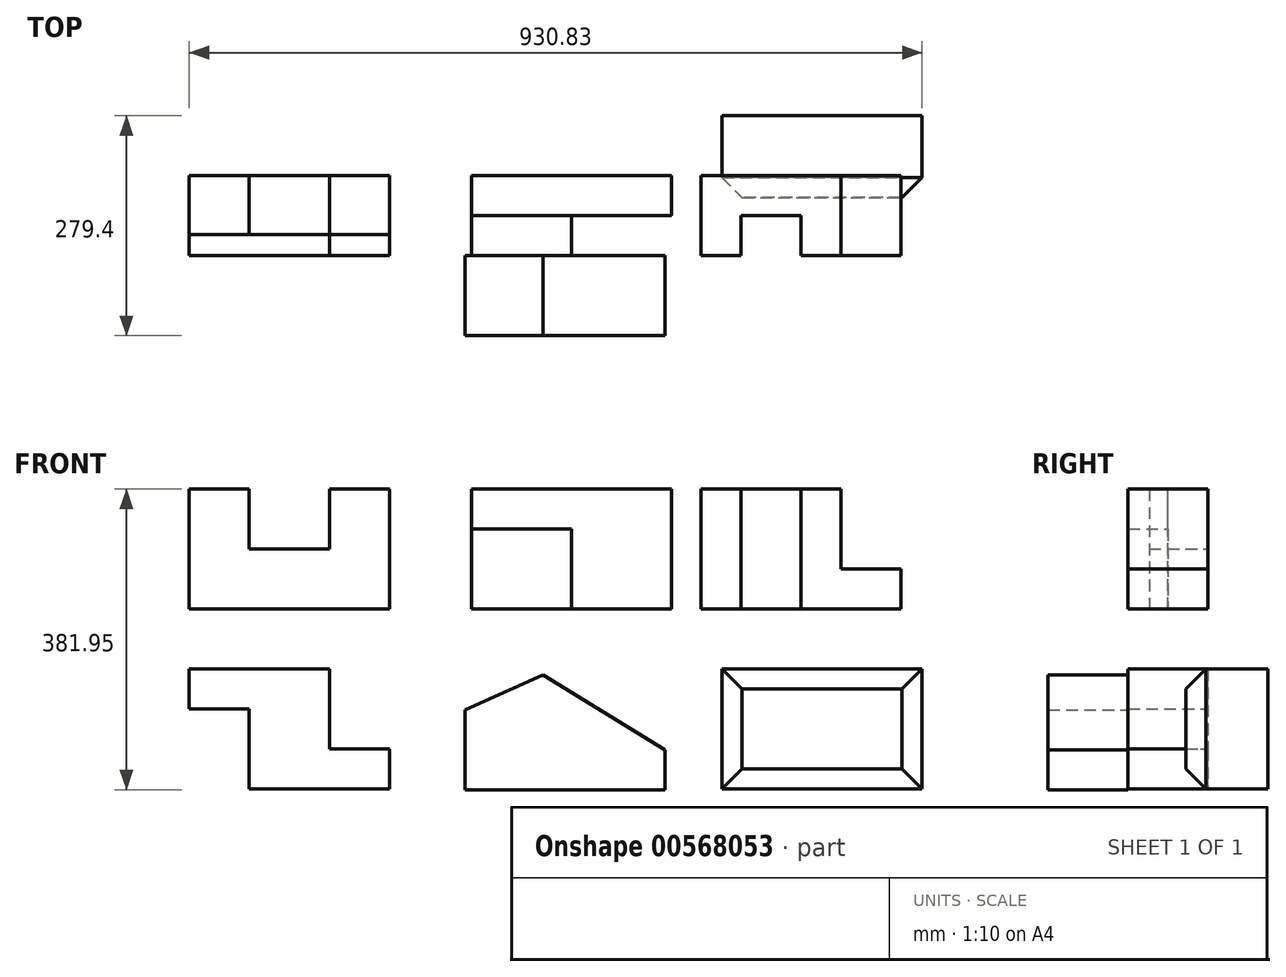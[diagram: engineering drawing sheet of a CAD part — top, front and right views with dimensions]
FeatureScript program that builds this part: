
annotation { "Feature Type Name" : "Feature", "Feature Type Description" : "" }
export const myFeature = defineFeature(function(context is Context, id is Id, definition is map)
    precondition{}
    {
        {
            var Q0;
            Q0=qCreatedBy(makeId("Front.planeOp"),FACE);
            var sketch = newSketch(context, id + "F0", { "sketchPlane" : qUnion([Q0])});
            skLineSegment(sketch, "E0", {"start": v(0, 0) * mm, "end": v(254, 0) * mm});
            skLineSegment(sketch, "E1", {"start": v(254, 0) * mm, "end": v(254, 152.4) * mm});
            skLineSegment(sketch, "E2", {"start": v(254, 152.4) * mm, "end": v(177.8, 152.4) * mm});
            skLineSegment(sketch, "E3", {"start": v(177.8, 152.4) * mm, "end": v(177.8, 76.2) * mm});
            skLineSegment(sketch, "E4", {"start": v(177.8, 76.2) * mm, "end": v(76.2, 76.2) * mm});
            skLineSegment(sketch, "E5", {"start": v(76.2, 76.2) * mm, "end": v(76.2, 152.4) * mm});
            skLineSegment(sketch, "E6", {"start": v(76.2, 152.4) * mm, "end": v(0, 152.4) * mm});
            skLineSegment(sketch, "E7", {"start": v(0, 152.4) * mm, "end": v(0, 0) * mm});
            skSolve(sketch);
        }
        {
            var Q0;
            Q0=makeQuery(id+"F0.imprint","IMPRINT",FACE,{"disambiguationData":[TD([[makeQuery(id+"F0.imprint","IMPRINT",EDGE,{"derivedFrom":sQuery(id+"F0.wireOp",EDGE,"E0")}),1.0]])]});
            extrude(context, id + "F1", {"entities" : qUnion([Q0]), "depth" : 74.68 * mm, "offsetDistance" : 25.4 * mm});
        }
        {
            var Q0;
            Q0=qCreatedBy(makeId("Top.planeOp"),FACE);
            var sketch = newSketch(context, id + "F2", { "sketchPlane" : qUnion([Q0])});
            skLineSegment(sketch, "E8", {"start": v(0, -98.1) * mm, "end": v(332.6, -98.1) * mm});
            skLineSegment(sketch, "E9", {"start": v(358.46, -101.6) * mm, "end": v(485.46, -101.6) * mm});
            skLineSegment(sketch, "E10", {"start": v(485.46, -101.6) * mm, "end": v(485.46, -50.8) * mm});
            skLineSegment(sketch, "E11", {"start": v(485.46, -50.8) * mm, "end": v(612.46, -50.8) * mm});
            skLineSegment(sketch, "E12", {"start": v(612.46, -50.8) * mm, "end": v(612.46, 0) * mm});
            skLineSegment(sketch, "E13", {"start": v(612.46, 0) * mm, "end": v(358.46, 0) * mm});
            skLineSegment(sketch, "E14", {"start": v(358.46, 0) * mm, "end": v(358.46, -101.6) * mm});
            skSolve(sketch);
        }
        {
            var Q0;
            Q0=qCreatedBy(makeId("Front.planeOp"),FACE);
            var sketch = newSketch(context, id + "F3", { "sketchPlane" : qUnion([Q0])});
            skLineSegment(sketch, "E15", {"start": v(649.95, 0) * mm, "end": v(649.95, 152.4) * mm});
            skLineSegment(sketch, "E16", {"start": v(649.95, 152.4) * mm, "end": v(827.75, 152.4) * mm});
            skLineSegment(sketch, "E17", {"start": v(827.75, 152.4) * mm, "end": v(827.75, 50.8) * mm});
            skLineSegment(sketch, "E18", {"start": v(827.75, 50.8) * mm, "end": v(903.95, 50.8) * mm});
            skLineSegment(sketch, "E19", {"start": v(903.95, 50.8) * mm, "end": v(903.95, 0) * mm});
            skLineSegment(sketch, "E20", {"start": v(903.95, 0) * mm, "end": v(649.95, 0) * mm});
            skSolve(sketch);
        }
        {
            var Q0;
            Q0=makeQuery(id+"F3.imprint","IMPRINT",FACE,{"disambiguationData":[TD([[makeQuery(id+"F3.imprint","IMPRINT",EDGE,{"derivedFrom":sQuery(id+"F3.wireOp",EDGE,"E15")}),-1.0]])]});
            extrude(context, id + "F4", {"entities" : qUnion([Q0]), "depth" : 101.6 * mm, "offsetDistance" : 25.4 * mm});
        }
        {
            var Q0;
            Q0=makeQuery(id+"F4.opExtrude","SWEPT_FACE",FACE,{"disambiguationData":[OSD([sQuery(id+"F3.wireOp",EDGE,"E16")])]});
            var sketch = newSketch(context, id + "F5", { "sketchPlane" : qUnion([Q0])});
            skLineSegment(sketch, "E21.bottom", {"start": v(700.75, -101.6) * mm, "end": v(776.95, -101.6) * mm});
            skLineSegment(sketch, "E21.top", {"start": v(700.75, -50.8) * mm, "end": v(776.95, -50.8) * mm});
            skLineSegment(sketch, "E21.left", {"start": v(700.75, -101.6) * mm, "end": v(700.75, -50.8) * mm});
            skLineSegment(sketch, "E21.right", {"start": v(776.95, -101.6) * mm, "end": v(776.95, -50.8) * mm});
            skSolve(sketch);
        }
        {
            var Q0;
            Q0=makeQuery(id+"F5.imprint","IMPRINT",FACE,{"disambiguationData":[TD([[makeQuery(id+"F5.imprint","IMPRINT",EDGE,{"derivedFrom":sQuery(id+"F5.wireOp",EDGE,"E21.bottom")}),1.0]])]});
            extrude(context, id + "F6", {"entities" : qUnion([Q0]), "operationType" : NewBodyOperationType.REMOVE, "oppositeDirection" : true, "depth" : 152.4 * mm, "offsetDistance" : 25.4 * mm});
        }
        {
            var Q0;
            Q0=makeQuery(id+"F2.imprint","IMPRINT",FACE,{"disambiguationData":[TD([[makeQuery(id+"F2.imprint","IMPRINT",EDGE,{"derivedFrom":sQuery(id+"F2.wireOp",EDGE,"E9")}),1.0]])]});
            extrude(context, id + "F7", {"entities" : qUnion([Q0]), "depth" : 152.4 * mm, "offsetDistance" : 25.4 * mm});
        }
        {
            var Q0;
            Q0=makeQuery(id+"F7.opExtrude","CAP_FACE",FACE,{"disambiguationData":[OSD([sQuery(id+"F2.wireOp",EDGE,"E9"),sQuery(id+"F2.wireOp",EDGE,"E10"),sQuery(id+"F2.wireOp",EDGE,"E11"),sQuery(id+"F2.wireOp",EDGE,"E12"),sQuery(id+"F2.wireOp",EDGE,"E13"),sQuery(id+"F2.wireOp",EDGE,"E14")])],"isStart":false});
            var sketch = newSketch(context, id + "F8", { "sketchPlane" : qUnion([Q0])});
            skLineSegment(sketch, "E22.bottom", {"start": v(485.46, -101.6) * mm, "end": v(358.46, -101.6) * mm});
            skLineSegment(sketch, "E22.top", {"start": v(485.46, -50.8) * mm, "end": v(358.46, -50.8) * mm});
            skLineSegment(sketch, "E22.left", {"start": v(485.46, -101.6) * mm, "end": v(485.46, -50.8) * mm});
            skLineSegment(sketch, "E22.right", {"start": v(358.46, -101.6) * mm, "end": v(358.46, -50.8) * mm});
            skSolve(sketch);
        }
        {
            var Q0;
            Q0=makeQuery(id+"F8.imprint","IMPRINT",FACE,{"disambiguationData":[TD([[makeQuery(id+"F8.imprint","IMPRINT",EDGE,{"derivedFrom":sQuery(id+"F8.wireOp",EDGE,"E22.bottom")}),1.0]])]});
            extrude(context, id + "F9", {"entities" : qUnion([Q0]), "operationType" : NewBodyOperationType.REMOVE, "oppositeDirection" : true, "depth" : 50.8 * mm, "offsetDistance" : 25.4 * mm});
        }
        {
            var Q0;
            Q0=qCreatedBy(makeId("Top.planeOp"),FACE);
            var sketch = newSketch(context, id + "F10", { "sketchPlane" : qUnion([Q0])});
            skLineSegment(sketch, "E23", {"start": v(0, 0) * mm, "end": v(0, -203.2) * mm});
            skLineSegment(sketch, "E24.bottom", {"start": v(0, -203.2) * mm, "end": v(254, -203.2) * mm});
            skLineSegment(sketch, "E24.top", {"start": v(0, -304.8) * mm, "end": v(254, -304.8) * mm});
            skLineSegment(sketch, "E24.left", {"start": v(0, -203.2) * mm, "end": v(0, -304.8) * mm});
            skLineSegment(sketch, "E24.right", {"start": v(254, -203.2) * mm, "end": v(254, -304.8) * mm});
            skSolve(sketch);
        }
        {
            var Q0;
            Q0=makeQuery(id+"F10.imprint","IMPRINT",FACE,{"disambiguationData":[TD([[makeQuery(id+"F10.imprint","IMPRINT",EDGE,{"derivedFrom":sQuery(id+"F10.wireOp",EDGE,"E24.bottom")}),-1.0]])]});
            extrude(context, id + "F11", {"entities" : qUnion([Q0]), "depth" : 152.4 * mm, "offsetDistance" : 25.4 * mm});
        }
        {
            var Q0;
            Q0=makeQuery(id+"F11.opExtrude","SWEPT_FACE",FACE,{"disambiguationData":[OSD([sQuery(id+"F10.wireOp",EDGE,"E24.top")])]});
            var sketch = newSketch(context, id + "F12", { "sketchPlane" : qUnion([Q0])});
            skLineSegment(sketch, "E25.bottom", {"start": v(0, 0) * mm, "end": v(76.2, 0) * mm});
            skLineSegment(sketch, "E25.top", {"start": v(0, 101.6) * mm, "end": v(76.2, 101.6) * mm});
            skLineSegment(sketch, "E25.left", {"start": v(0, 0) * mm, "end": v(0, 101.6) * mm});
            skLineSegment(sketch, "E25.right", {"start": v(76.2, 0) * mm, "end": v(76.2, 101.6) * mm});
            skSolve(sketch);
        }
        {
            var Q0;
            Q0=makeQuery(id+"F12.imprint","IMPRINT",FACE,{"disambiguationData":[TD([[makeQuery(id+"F12.imprint","IMPRINT",EDGE,{"derivedFrom":sQuery(id+"F12.wireOp",EDGE,"E25.bottom")}),1.0]])]});
            extrude(context, id + "F13", {"entities" : qUnion([Q0]), "operationType" : NewBodyOperationType.REMOVE, "oppositeDirection" : true, "depth" : 101.6 * mm, "offsetDistance" : 25.4 * mm});
        }
        {
            var Q0;
            Q0=makeQuery(id+"F11.opExtrude","SWEPT_FACE",FACE,{"disambiguationData":[OSD([sQuery(id+"F10.wireOp",EDGE,"E24.top")])]});
            var sketch = newSketch(context, id + "F14", { "sketchPlane" : qUnion([Q0])});
            skLineSegment(sketch, "E26.bottom", {"start": v(254, 152.4) * mm, "end": v(177.8, 152.4) * mm});
            skLineSegment(sketch, "E26.top", {"start": v(254, 50.8) * mm, "end": v(177.8, 50.8) * mm});
            skLineSegment(sketch, "E26.left", {"start": v(254, 152.4) * mm, "end": v(254, 50.8) * mm});
            skLineSegment(sketch, "E26.right", {"start": v(177.8, 152.4) * mm, "end": v(177.8, 50.8) * mm});
            skSolve(sketch);
        }
        {
            var Q0;
            Q0=makeQuery(id+"F14.imprint","IMPRINT",FACE,{"disambiguationData":[TD([[makeQuery(id+"F14.imprint","IMPRINT",EDGE,{"derivedFrom":sQuery(id+"F14.wireOp",EDGE,"E26.bottom")}),-1.0]])]});
            extrude(context, id + "F15", {"entities" : qUnion([Q0]), "operationType" : NewBodyOperationType.REMOVE, "oppositeDirection" : true, "depth" : 101.6 * mm, "offsetDistance" : 25.4 * mm});
        }
        {
            var Q0;
            Q0=makeQuery(id+"F11.opExtrude","SWEPT_BODY",BODY,{"disambiguationData":[OSD([sQuery(id+"F10.wireOp",EDGE,"E24.bottom"),sQuery(id+"F10.wireOp",EDGE,"E24.top"),sQuery(id+"F10.wireOp",EDGE,"E24.left"),sQuery(id+"F10.wireOp",EDGE,"E24.right")])]});
            deleteBodies(context, id + "F16", {"entities" : qUnion([Q0])});
        }
        {
            var Q0;
            Q0=qCreatedBy(makeId("Front.planeOp"),FACE);
            var sketch = newSketch(context, id + "F17", { "sketchPlane" : qUnion([Q0])});
            skLineSegment(sketch, "E27", {"start": v(0, -76.2) * mm, "end": v(177.8, -76.2) * mm});
            skLineSegment(sketch, "E28", {"start": v(177.8, -76.2) * mm, "end": v(177.8, -177.8) * mm});
            skLineSegment(sketch, "E29", {"start": v(177.8, -177.8) * mm, "end": v(254, -177.8) * mm});
            skLineSegment(sketch, "E30", {"start": v(254, -177.8) * mm, "end": v(254, -228.6) * mm});
            skLineSegment(sketch, "E31", {"start": v(254, -228.6) * mm, "end": v(76.2, -228.6) * mm});
            skLineSegment(sketch, "E32", {"start": v(76.2, -228.6) * mm, "end": v(76.2, -127) * mm});
            skLineSegment(sketch, "E33", {"start": v(76.2, -127) * mm, "end": v(0, -127) * mm});
            skLineSegment(sketch, "E34", {"start": v(0, -127) * mm, "end": v(0, -76.2) * mm});
            skSolve(sketch);
        }
        {
            var Q0;
            Q0=makeQuery(id+"F17.imprint","IMPRINT",FACE,{"disambiguationData":[TD([[makeQuery(id+"F17.imprint","IMPRINT",EDGE,{"derivedFrom":sQuery(id+"F17.wireOp",EDGE,"E27")}),-1.0]])]});
            extrude(context, id + "F18", {"entities" : qUnion([Q0]), "depth" : 101.6 * mm, "offsetDistance" : 25.4 * mm});
        }
        {
            var Q0;
            Q0=makeQuery(id+"F18.opExtrude","CAP_FACE",FACE,{"disambiguationData":[OSD([sQuery(id+"F17.wireOp",EDGE,"E27"),sQuery(id+"F17.wireOp",EDGE,"E28"),sQuery(id+"F17.wireOp",EDGE,"E29"),sQuery(id+"F17.wireOp",EDGE,"E30"),sQuery(id+"F17.wireOp",EDGE,"E31"),sQuery(id+"F17.wireOp",EDGE,"E32"),sQuery(id+"F17.wireOp",EDGE,"E33"),sQuery(id+"F17.wireOp",EDGE,"E34")])],"isStart":false});
            var sketch = newSketch(context, id + "F19", { "sketchPlane" : qUnion([Q0])});
            skLineSegment(sketch, "E35", {"start": v(349.97, -229.55) * mm, "end": v(349.97, -127.95) * mm});
            skLineSegment(sketch, "E36", {"start": v(349.97, -127.95) * mm, "end": v(449.1, -83.55) * mm});
            skLineSegment(sketch, "E37", {"start": v(449.1, -83.55) * mm, "end": v(603.97, -178.75) * mm});
            skLineSegment(sketch, "E38", {"start": v(603.97, -178.75) * mm, "end": v(603.97, -229.55) * mm});
            skLineSegment(sketch, "E39", {"start": v(603.97, -229.55) * mm, "end": v(349.97, -229.55) * mm});
            skSolve(sketch);
        }
        {
            var Q0;
            Q0=makeQuery(id+"F19.imprint","IMPRINT",FACE,{"disambiguationData":[TD([[makeQuery(id+"F19.imprint","IMPRINT",EDGE,{"derivedFrom":sQuery(id+"F19.wireOp",EDGE,"E35")}),-1.0]])]});
            extrude(context, id + "F20", {"entities" : qUnion([Q0]), "depth" : 101.6 * mm, "offsetDistance" : 25.4 * mm});
        }
        {
            var Q0;
            Q0=qCreatedBy(makeId("Front.planeOp"),FACE);
            var sketch = newSketch(context, id + "F21", { "sketchPlane" : qUnion([Q0])});
            skLineSegment(sketch, "E40", {"start": v(676.83, -228.54) * mm, "end": v(676.83, -76.14) * mm});
            skLineSegment(sketch, "E41", {"start": v(676.83, -76.14) * mm, "end": v(930.83, -76.14) * mm});
            skLineSegment(sketch, "E42", {"start": v(930.83, -76.14) * mm, "end": v(930.83, -228.54) * mm});
            skLineSegment(sketch, "E43", {"start": v(930.83, -228.54) * mm, "end": v(676.83, -228.54) * mm});
            skSolve(sketch);
        }
        {
            var Q0;
            Q0=makeQuery(id+"F21.imprint","IMPRINT",FACE,{"disambiguationData":[TD([[makeQuery(id+"F21.imprint","IMPRINT",EDGE,{"derivedFrom":sQuery(id+"F21.wireOp",EDGE,"E40")}),-1.0]])]});
            extrude(context, id + "F22", {"entities" : qUnion([Q0]), "depth" : 27.94 * mm, "offsetDistance" : 25.4 * mm});
        }
        {
            var Q0;
            Q0=makeQuery(id+"F22.opExtrude","CAP_FACE",FACE,{"disambiguationData":[OSD([sQuery(id+"F21.wireOp",EDGE,"E40"),sQuery(id+"F21.wireOp",EDGE,"E41"),sQuery(id+"F21.wireOp",EDGE,"E42"),sQuery(id+"F21.wireOp",EDGE,"E43")])],"isStart":false});
            chamfer(context, id + "F23", {"entities" : qUnion([Q0]), "width" : 25.4 * mm, "tangentPropagation" : true});
        }
        {
            var Q0;
            Q0 = qSketchRegion(id + "F21", true);
            extrude(context, id + "F24", {"entities" : qUnion([Q0]), "operationType" : NewBodyOperationType.ADD, "oppositeDirection" : true, "depth" : 76.2 * mm, "offsetDistance" : 25.4 * mm});
        }
    });
